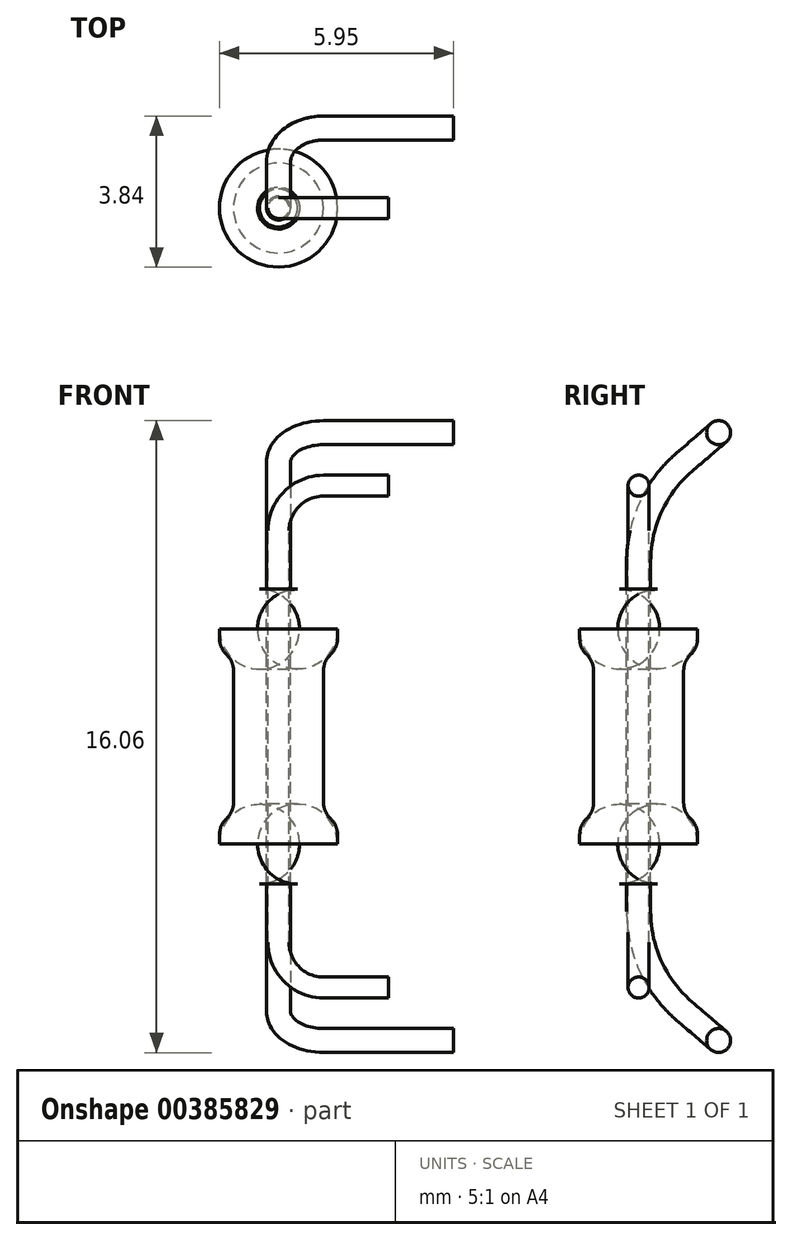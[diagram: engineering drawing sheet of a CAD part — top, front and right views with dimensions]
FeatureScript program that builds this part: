
annotation { "Feature Type Name" : "Feature", "Feature Type Description" : "" }
export const myFeature = defineFeature(function(context is Context, id is Id, definition is map)
    precondition{}
    {
        {
            var Q0;
            Q0=qCreatedBy(makeId("Front.planeOp"),FACE);
            var sketch = newSketch(context, id + "F0", { "sketchPlane" : qUnion([Q0])});
            skLineSegment(sketch, "E0", {"start": v(0, 3.75) * mm, "end": v(1.5, 3.75) * mm});
            skLineSegment(sketch, "E1", {"start": v(1.5, 3.75) * mm, "end": v(1.5, 2.26) * mm});
            skLineSegment(sketch, "E2", {"start": v(1.5, 2.26) * mm, "end": v(1.14, 1.9) * mm});
            skLineSegment(sketch, "E3", {"start": v(1.14, 1.9) * mm, "end": v(1.14, -1.9) * mm});
            skLineSegment(sketch, "E4", {"start": v(1.14, -1.9) * mm, "end": v(1.5, -2.26) * mm});
            skLineSegment(sketch, "E5", {"start": v(1.5, -2.26) * mm, "end": v(1.5, -3.75) * mm});
            skLineSegment(sketch, "E6", {"start": v(1.5, -3.75) * mm, "end": v(0, -3.75) * mm});
            skLineSegment(sketch, "E7", {"start": v(0, -3.75) * mm, "end": v(0, 3.75) * mm});
            skLineSegment(sketch, "E8", {"start": v(0, 3.75) * mm, "end": v(-1.5, 3.75) * mm, "construction": true});
            skLineSegment(sketch, "E9", {"start": v(1.14, 0) * mm, "end": v(0, 0) * mm, "construction": true});
            skLineSegment(sketch, "E10", {"start": v(0, 0) * mm, "end": v(-1.14, 0) * mm, "construction": true});
            skSolve(sketch);
        }
        {
            var Q0;
            Q0=makeQuery(id+"F0.imprint","IMPRINT",FACE,{"disambiguationData":[TD([[makeQuery(id+"F0.imprint","IMPRINT",EDGE,{"derivedFrom":sQuery(id+"F0.wireOp",EDGE,"E0")}),-1.0]])]});
            var Q1;
            Q1=sQuery(id+"F0.wireOp",EDGE,"E7");
            revolve(context, id + "F1", {"entities" : qUnion([Q0]), "axis" : qUnion([Q1]), "revolveType" : RevolveType.FULL});
        }
        {
            var Q0;
            Q0=makeQuery(id+"F1.opRevolve","SWEPT_EDGE",EDGE,{"disambiguationData":[OSD([sQuery(id+"F0.wireOp",EDGE,"E0"),sQuery(id+"F0.wireOp",EDGE,"E1")])]});
            var Q1;
            Q1=makeQuery(id+"F1.opRevolve","SWEPT_EDGE",EDGE,{"disambiguationData":[OSD([sQuery(id+"F0.wireOp",EDGE,"E5"),sQuery(id+"F0.wireOp",EDGE,"E6")])]});
            fillet(context, id + "F2", {"entities" : qUnion([Q0, Q1]), "radius" : 1.02 * mm, "tangentPropagation" : true, "allowEdgeOverflow" : false});
        }
        {
            var Q0;
            Q0=makeQuery(id+"F1.opRevolve","SWEPT_EDGE",EDGE,{"disambiguationData":[OSD([sQuery(id+"F0.wireOp",EDGE,"E1"),sQuery(id+"F0.wireOp",EDGE,"E2")])]});
            var Q1;
            Q1=makeQuery(id+"F1.opRevolve","SWEPT_EDGE",EDGE,{"disambiguationData":[OSD([sQuery(id+"F0.wireOp",EDGE,"E2"),sQuery(id+"F0.wireOp",EDGE,"E3")])]});
            var Q2;
            Q2=makeQuery(id+"F1.opRevolve","SWEPT_EDGE",EDGE,{"disambiguationData":[OSD([sQuery(id+"F0.wireOp",EDGE,"E3"),sQuery(id+"F0.wireOp",EDGE,"E4")])]});
            var Q3;
            Q3=makeQuery(id+"F1.opRevolve","SWEPT_EDGE",EDGE,{"disambiguationData":[OSD([sQuery(id+"F0.wireOp",EDGE,"E4"),sQuery(id+"F0.wireOp",EDGE,"E5")])]});
            fillet(context, id + "F3", {"entities" : qUnion([Q0, Q1, Q2, Q3]), "radius" : 0.56 * mm, "tangentPropagation" : true, "allowEdgeOverflow" : false});
        }
        {
            var Q0;
            Q0=qCreatedBy(makeId("Front.planeOp"),FACE);
            cPlane(context, id + "F4", {"entities" : qUnion([Q0]), "cplaneType" : CPlaneType.OFFSET, "offset" : 2.03 * mm, "oppositeDirection" : true, "width" : 152.4 * mm, "height" : 152.4 * mm});
        }
        {
            var Q0;
            Q0=qCreatedBy(id+"F4.planeOp",FACE);
            var sketch = newSketch(context, id + "F5", { "sketchPlane" : qUnion([Q0])});
            skPoint(sketch, "E11", {"position": v(4.45, 7.72) * mm});
            skPoint(sketch, "E12", {"position": v(1.14, -7.72) * mm});
            skPoint(sketch, "E13", {"position": v(4.45, -7.72) * mm});
            skLineSegment(sketch, "E14", {"start": v(4.45, 7.72) * mm, "end": v(1.14, 7.72) * mm});
            skLineSegment(sketch, "E15", {"start": v(4.45, -7.72) * mm, "end": v(1.14, -7.72) * mm});
            skLineSegment(sketch, "E16", {"start": v(4.45, 7.72) * mm, "end": v(4.45, 0) * mm, "construction": true});
            skLineSegment(sketch, "E17", {"start": v(4.45, -7.72) * mm, "end": v(4.45, 0) * mm, "construction": true});
            skSolve(sketch);
        }
        {
            var Q0;
            Q0=qCreatedBy(makeId("Right.planeOp"),FACE);
            var Q1;
            Q1=sQuery(id+"F5.wireOp",VERTEX,"E13");
            cPlane(context, id + "F6", {"entities" : qUnion([Q0, Q1]), "cplaneType" : CPlaneType.PLANE_POINT, "offset" : 25.4 * mm, "width" : 152.4 * mm, "height" : 152.4 * mm});
        }
        {
            var Q0;
            Q0=qCreatedBy(id+"F6.planeOp",FACE);
            var sketch = newSketch(context, id + "F7", { "sketchPlane" : qUnion([Q0])});
            skPoint(sketch, "E18.0", {"position": v(2.03, -7.72) * mm});
            skCircle(sketch, "E19", {"center": v(2.03, -7.72) * mm, "radius": 0.3 * mm});
            skSolve(sketch);
        }
        {
            var Q0;
            Q0=qCreatedBy(makeId("Right.planeOp"),FACE);
            var sketch = newSketch(context, id + "F8", { "sketchPlane" : qUnion([Q0])});
            skPoint(sketch, "E20", {"position": v(0, 4.45) * mm});
            skPoint(sketch, "E21", {"position": v(1.16, 6.98) * mm});
            skPoint(sketch, "E22.0", {"position": v(2.03, 7.72) * mm});
            skLineSegment(sketch, "E23", {"start": v(2.03, 7.72) * mm, "end": v(1.16, 6.98) * mm, "construction": true});
            skLineSegment(sketch, "E24", {"start": v(1.16, 6.98) * mm, "end": v(1.16, 0) * mm, "construction": true});
            skLineSegment(sketch, "E25", {"start": v(0, 0) * mm, "end": v(0, -4.45) * mm});
            skPoint(sketch, "E26", {"position": v(0, -4.45) * mm});
            skPoint(sketch, "E27", {"position": v(1.16, -6.98) * mm});
            skPoint(sketch, "E28.0", {"position": v(2.03, -7.72) * mm});
            skLineSegment(sketch, "E29", {"start": v(2.03, -7.72) * mm, "end": v(1.16, -6.98) * mm, "construction": true});
            skLineSegment(sketch, "E30", {"start": v(1.16, -6.98) * mm, "end": v(1.16, 0) * mm, "construction": true});
            skLineSegment(sketch, "E31", {"start": v(0, 0) * mm, "end": v(0, 4.45) * mm});
            skArc(sketch, "E32", {"start": v(0, -4.45) * mm, "mid": v(0.3, -5.84) * mm, "end": v(1.16, -6.98) * mm});
            skArc(sketch, "E33", {"start": v(1.16, 6.98) * mm, "mid": v(0.3, 5.84) * mm, "end": v(0, 4.44) * mm});
            skSolve(sketch);
        }
        {
            var Q0;
            Q0=sQuery(id+"F8.wireOp",VERTEX,"E21");
            var Q1;
            Q1=sQuery(id+"F5.wireOp",VERTEX,"E14.end");
            var Q2;
            Q2=sQuery(id+"F5.wireOp",VERTEX,"E11");
            cPlane(context, id + "F9", {"entities" : qUnion([Q0, Q1, Q2]), "cplaneType" : CPlaneType.THREE_POINT, "offset" : 25.4 * mm, "width" : 152.4 * mm, "height" : 152.4 * mm});
        }
        {
            var Q0;
            Q0=qCreatedBy(id+"F9.planeOp",FACE);
            var sketch = newSketch(context, id + "F10", { "sketchPlane" : qUnion([Q0])});
            skPoint(sketch, "E34.0", {"position": v(0, 5.43) * mm});
            skPoint(sketch, "E35.0", {"position": v(1.14, 6.57) * mm});
            skLineSegment(sketch, "E36.0", {"start": v(4.45, 6.57) * mm, "end": v(1.14, 6.57) * mm, "construction": true});
            skLineSegment(sketch, "E37.0", {"start": v(0, 5.43) * mm, "end": v(0, 2.9) * mm, "construction": true});
            skArc(sketch, "E38", {"start": v(1.14, 6.57) * mm, "mid": v(0.33, 6.23) * mm, "end": v(0, 5.43) * mm});
            skSolve(sketch);
        }
        {
            var Q0;
            Q0=sQuery(id+"F5.wireOp",VERTEX,"E12");
            var Q1;
            Q1=sQuery(id+"F8.wireOp",VERTEX,"E27");
            var Q2;
            Q2=sQuery(id+"F7.wireOp",VERTEX,"E18.0");
            cPlane(context, id + "F11", {"entities" : qUnion([Q0, Q1, Q2]), "cplaneType" : CPlaneType.THREE_POINT, "offset" : 25.4 * mm, "width" : 152.4 * mm, "height" : 152.4 * mm});
        }
        {
            var Q0;
            Q0=qCreatedBy(id+"F11.planeOp",FACE);
            var sketch = newSketch(context, id + "F12", { "sketchPlane" : qUnion([Q0])});
            skLineSegment(sketch, "E39.0", {"start": v(4.44, -6.57) * mm, "end": v(1.14, -6.57) * mm, "construction": true});
            skPoint(sketch, "E40.0", {"position": v(1.14, -6.57) * mm});
            skPoint(sketch, "E41.0", {"position": v(0, -5.43) * mm});
            skLineSegment(sketch, "E42.0", {"start": v(0, -2.9) * mm, "end": v(0, -5.43) * mm, "construction": true});
            skArc(sketch, "E43", {"start": v(0, -5.43) * mm, "mid": v(0.33, -6.23) * mm, "end": v(1.14, -6.57) * mm});
            skSolve(sketch);
        }
        {
            var Q0;
            Q0=makeQuery(id+"F7.imprint","IMPRINT",FACE,{"disambiguationData":[TD([[makeQuery(id+"F7.imprint","IMPRINT",EDGE,{"derivedFrom":sQuery(id+"F7.wireOp",EDGE,"E19")}),1.0]])]});
            var Q1;
            Q1=sQuery(id+"F5.wireOp",EDGE,"E15");
            var Q2;
            Q2=sQuery(id+"F12.wireOp",EDGE,"E43");
            var Q3;
            Q3=sQuery(id+"F8.wireOp",EDGE,"E32");
            var Q4;
            Q4=sQuery(id+"F8.wireOp",EDGE,"E25");
            var Q5;
            Q5=sQuery(id+"F8.wireOp",EDGE,"E31");
            var Q6;
            Q6=sQuery(id+"F8.wireOp",EDGE,"E33");
            var Q7;
            Q7=sQuery(id+"F10.wireOp",EDGE,"E38");
            var Q8;
            Q8=sQuery(id+"F5.wireOp",EDGE,"E14");
            sweep(context, id + "F13", {"profiles" : qUnion([Q0]), "path" : qUnion([Q1, Q2, Q3, Q4, Q5, Q6, Q7, Q8])});
        }
        {
            var Q0;
            Q0=qCreatedBy(makeId("Front.planeOp"),FACE);
            var sketch = newSketch(context, id + "F14", { "sketchPlane" : qUnion([Q0])});
            skLineSegment(sketch, "E44", {"start": v(0, 0) * mm, "end": v(0, 5.23) * mm});
            skLineSegment(sketch, "E45", {"start": v(2.8, 6.38) * mm, "end": v(1.14, 6.38) * mm});
            skArc(sketch, "E46", {"start": v(1.14, 6.38) * mm, "mid": v(0.33, 6.04) * mm, "end": v(0, 5.23) * mm});
            skLineSegment(sketch, "E47.MirrorCS", {"start": v(2.8, -6.38) * mm, "end": v(1.14, -6.38) * mm});
            skArc(sketch, "E48.MirrorCS", {"start": v(1.14, -6.38) * mm, "mid": v(0.33, -6.04) * mm, "end": v(0, -5.23) * mm});
            skLineSegment(sketch, "E49.MirrorCS", {"start": v(0, 0) * mm, "end": v(0, -5.23) * mm});
            skSolve(sketch);
        }
        {
            var Q0;
            Q0=qCreatedBy(makeId("Right.planeOp"),FACE);
            var Q1;
            Q1=sQuery(id+"F14.wireOp",VERTEX,"E47.MirrorCS.start");
            cPlane(context, id + "F15", {"entities" : qUnion([Q0, Q1]), "cplaneType" : CPlaneType.PLANE_POINT, "offset" : 25.4 * mm, "width" : 152.4 * mm, "height" : 152.4 * mm});
        }
        {
            var Q0;
            Q0=qCreatedBy(id+"F15.planeOp",FACE);
            var sketch = newSketch(context, id + "F16", { "sketchPlane" : qUnion([Q0])});
            skPoint(sketch, "E50.0", {"position": v(0, -6.38) * mm});
            skCircle(sketch, "E51", {"center": v(0, -6.38) * mm, "radius": 0.27 * mm});
            skSolve(sketch);
        }
        {
            var Q0;
            Q0=makeQuery(id+"F16.imprint","IMPRINT",FACE,{"disambiguationData":[TD([[makeQuery(id+"F16.imprint","IMPRINT",EDGE,{"derivedFrom":sQuery(id+"F16.wireOp",EDGE,"E51")}),1.0]])]});
            var Q1;
            Q1 = qConstructionFilter(qBodyType(qCreatedBy(id + "F14" ,EDGE), BodyType.WIRE), ConstructionObject.NO);
            sweep(context, id + "F17", {"profiles" : qUnion([Q0]), "path" : qUnion([Q1])});
        }
    });
